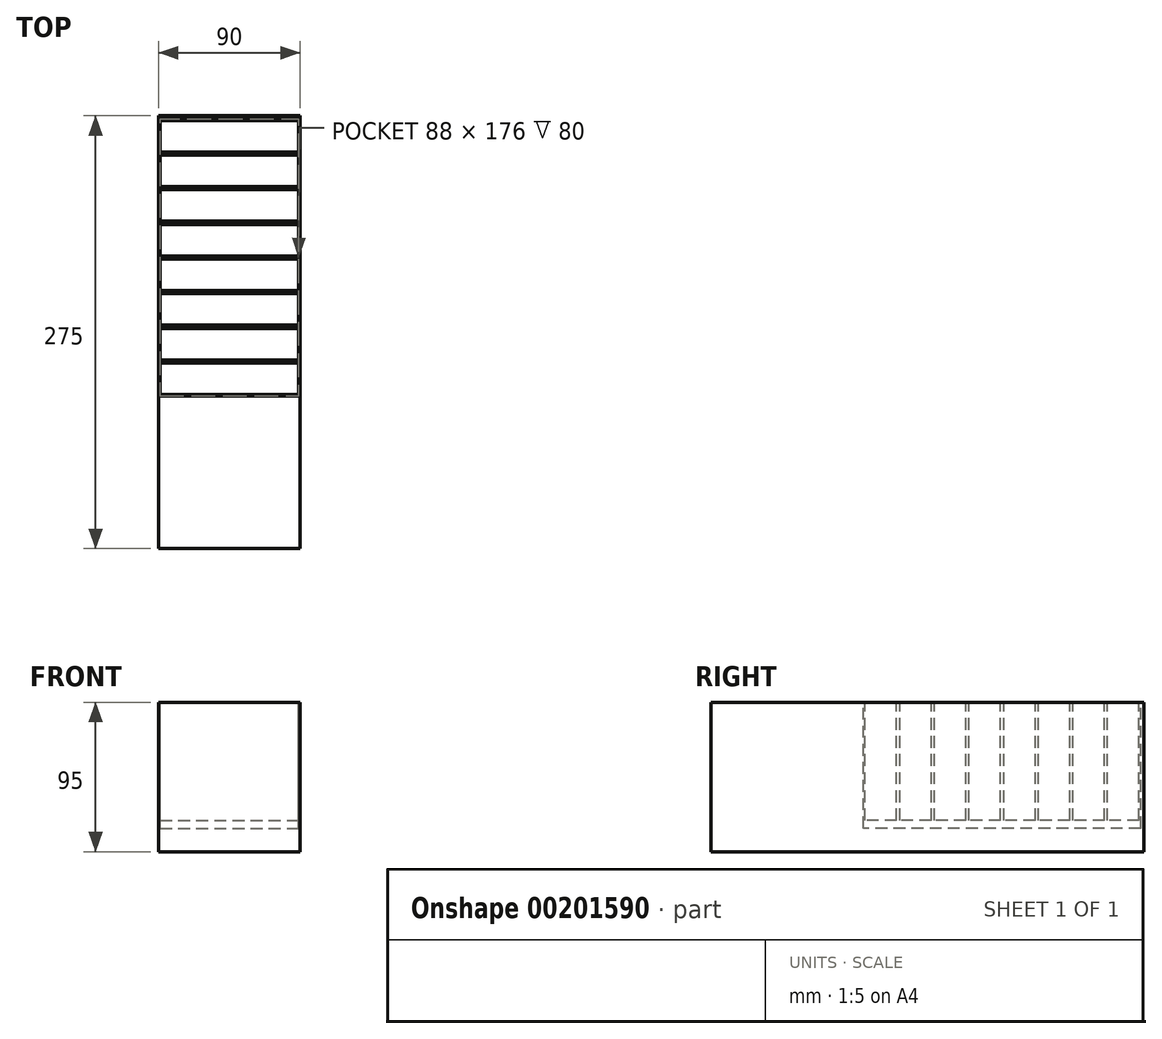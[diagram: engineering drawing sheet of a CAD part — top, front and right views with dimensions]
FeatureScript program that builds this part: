
annotation { "Feature Type Name" : "Feature", "Feature Type Description" : "" }
export const myFeature = defineFeature(function(context is Context, id is Id, definition is map)
    precondition{}
    {
        {
            var Q0;
            Q0=qCreatedBy(makeId("Front.planeOp"),FACE);
            var sketch = newSketch(context, id + "F0", { "sketchPlane" : qUnion([Q0])});
            skLineSegment(sketch, "E0.bottom", {"start": v(-45, 0) * mm, "end": v(45, 0) * mm});
            skLineSegment(sketch, "E0.top", {"start": v(-45, -95) * mm, "end": v(45, -95) * mm});
            skLineSegment(sketch, "E0.left", {"start": v(-45, 0) * mm, "end": v(-45, -95) * mm});
            skLineSegment(sketch, "E0.right", {"start": v(45, 0) * mm, "end": v(45, -95) * mm});
            skLineSegment(sketch, "E1", {"start": v(-45, 0) * mm, "end": v(45, -95) * mm, "construction": true});
            skSolve(sketch);
        }
        {
            var Q0;
            Q0 = qSketchRegion(id + "F0", true);
            extrude(context, id + "F1", {"entities" : qUnion([Q0]), "depth" : 275 * mm});
        }
        {
            var Q0;
            Q0=makeQuery(id+"F1.opExtrude","SWEPT_FACE",FACE,{"disambiguationData":[OSD([sQuery(id+"F0.wireOp",EDGE,"E0.bottom")])]});
            var sketch = newSketch(context, id + "F2", { "sketchPlane" : qUnion([Q0])});
            skLineSegment(sketch, "E2.bottom", {"start": v(-44, -2) * mm, "end": v(44, -2) * mm});
            skLineSegment(sketch, "E2.top", {"start": v(-44, -24) * mm, "end": v(44, -24) * mm, "construction": true});
            skLineSegment(sketch, "E2.left", {"start": v(-44, -2) * mm, "end": v(-44, -24) * mm});
            skLineSegment(sketch, "E2.right", {"start": v(44, -2) * mm, "end": v(44, -24) * mm});
            skLineSegment(sketch, "E3", {"start": v(-44, -24) * mm, "end": v(-44, -46) * mm});
            skLineSegment(sketch, "E4", {"start": v(-44, -46) * mm, "end": v(-44, -68) * mm});
            skLineSegment(sketch, "E5", {"start": v(-44, -68) * mm, "end": v(-44, -90) * mm});
            skLineSegment(sketch, "E6", {"start": v(-44, -90) * mm, "end": v(-44, -112) * mm});
            skLineSegment(sketch, "E7", {"start": v(-44, -112) * mm, "end": v(-44, -134) * mm});
            skLineSegment(sketch, "E8", {"start": v(-44, -134) * mm, "end": v(-44, -156) * mm});
            skLineSegment(sketch, "E9", {"start": v(-44, -156) * mm, "end": v(-44, -178) * mm});
            skLineSegment(sketch, "E10", {"start": v(0, 0) * mm, "end": v(0, -194.6) * mm, "construction": true});
            skLineSegment(sketch, "E11.MirrorCS", {"start": v(44, -156) * mm, "end": v(44, -178) * mm});
            skLineSegment(sketch, "E12.MirrorCS", {"start": v(44, -68) * mm, "end": v(44, -90) * mm});
            skLineSegment(sketch, "E13.MirrorCS", {"start": v(44, -24) * mm, "end": v(44, -46) * mm});
            skLineSegment(sketch, "E14.MirrorCS", {"start": v(44, -112) * mm, "end": v(44, -134) * mm});
            skLineSegment(sketch, "E15.MirrorCS", {"start": v(44, -134) * mm, "end": v(44, -156) * mm});
            skLineSegment(sketch, "E16.MirrorCS", {"start": v(44, -90) * mm, "end": v(44, -112) * mm});
            skLineSegment(sketch, "E17.MirrorCS", {"start": v(44, -46) * mm, "end": v(44, -68) * mm});
            skLineSegment(sketch, "E18", {"start": v(-44, -46) * mm, "end": v(44, -46) * mm, "construction": true});
            skLineSegment(sketch, "E19", {"start": v(-44, -68) * mm, "end": v(44, -68) * mm, "construction": true});
            skLineSegment(sketch, "E20", {"start": v(-44, -90) * mm, "end": v(44, -90) * mm, "construction": true});
            skLineSegment(sketch, "E21", {"start": v(-44, -112) * mm, "end": v(44, -112) * mm, "construction": true});
            skLineSegment(sketch, "E22", {"start": v(44, -134) * mm, "end": v(-44, -134) * mm, "construction": true});
            skLineSegment(sketch, "E23", {"start": v(-44, -156) * mm, "end": v(44, -156) * mm, "construction": true});
            skLineSegment(sketch, "E24", {"start": v(44, -178) * mm, "end": v(-44, -178) * mm});
            skSolve(sketch);
        }
        {
            var Q0;
            Q0 = qSketchRegion(id + "F2", true);
            extrude(context, id + "F3", {"entities" : qUnion([Q0]), "operationType" : NewBodyOperationType.REMOVE, "oppositeDirection" : true, "depth" : 80 * mm});
        }
        {
            var Q0;
            Q0=qCreatedBy(makeId("Top.planeOp"),FACE);
            var sketch = newSketch(context, id + "F4", { "sketchPlane" : qUnion([Q0])});
            skLineSegment(sketch, "E25.bottom", {"start": v(-44, -3) * mm, "end": v(44, -3) * mm});
            skLineSegment(sketch, "E25.top", {"start": v(-44, -23) * mm, "end": v(44, -23) * mm});
            skLineSegment(sketch, "E25.left", {"start": v(-44, -3) * mm, "end": v(-44, -23) * mm});
            skLineSegment(sketch, "E25.right", {"start": v(44, -3) * mm, "end": v(44, -23) * mm});
            skLineSegment(sketch, "E26", {"start": v(-44, -13) * mm, "end": v(44, -13) * mm, "construction": true});
            skLineSegment(sketch, "E27.0.1.0", {"start": v(-44, -25) * mm, "end": v(44, -25) * mm});
            skLineSegment(sketch, "E27.0.1.1", {"start": v(-44, -25) * mm, "end": v(-44, -45) * mm});
            skLineSegment(sketch, "E27.0.1.2", {"start": v(-44, -45) * mm, "end": v(44, -45) * mm});
            skLineSegment(sketch, "E27.0.1.3", {"start": v(44, -25) * mm, "end": v(44, -45) * mm});
            skLineSegment(sketch, "E27.0.2.0", {"start": v(-44, -47) * mm, "end": v(44, -47) * mm});
            skLineSegment(sketch, "E27.0.2.1", {"start": v(-44, -47) * mm, "end": v(-44, -67) * mm});
            skLineSegment(sketch, "E27.0.2.2", {"start": v(-44, -67) * mm, "end": v(44, -67) * mm});
            skLineSegment(sketch, "E27.0.2.3", {"start": v(44, -47) * mm, "end": v(44, -67) * mm});
            skLineSegment(sketch, "E27.0.3.0", {"start": v(-44, -69) * mm, "end": v(44, -69) * mm});
            skLineSegment(sketch, "E27.0.3.1", {"start": v(-44, -69) * mm, "end": v(-44, -89) * mm});
            skLineSegment(sketch, "E27.0.3.2", {"start": v(-44, -89) * mm, "end": v(44, -89) * mm});
            skLineSegment(sketch, "E27.0.3.3", {"start": v(44, -69) * mm, "end": v(44, -89) * mm});
            skLineSegment(sketch, "E27.0.4.0", {"start": v(-44, -91) * mm, "end": v(44, -91) * mm});
            skLineSegment(sketch, "E27.0.4.1", {"start": v(-44, -91) * mm, "end": v(-44, -111) * mm});
            skLineSegment(sketch, "E27.0.4.2", {"start": v(-44, -111) * mm, "end": v(44, -111) * mm});
            skLineSegment(sketch, "E27.0.4.3", {"start": v(44, -91) * mm, "end": v(44, -111) * mm});
            skLineSegment(sketch, "E27.0.5.0", {"start": v(-44, -113) * mm, "end": v(44, -113) * mm});
            skLineSegment(sketch, "E27.0.5.1", {"start": v(-44, -113) * mm, "end": v(-44, -133) * mm});
            skLineSegment(sketch, "E27.0.5.2", {"start": v(-44, -133) * mm, "end": v(44, -133) * mm});
            skLineSegment(sketch, "E27.0.5.3", {"start": v(44, -113) * mm, "end": v(44, -133) * mm});
            skLineSegment(sketch, "E27.0.6.0", {"start": v(-44, -135) * mm, "end": v(44, -135) * mm});
            skLineSegment(sketch, "E27.0.6.1", {"start": v(-44, -135) * mm, "end": v(-44, -155) * mm});
            skLineSegment(sketch, "E27.0.6.2", {"start": v(-44, -155) * mm, "end": v(44, -155) * mm});
            skLineSegment(sketch, "E27.0.6.3", {"start": v(44, -135) * mm, "end": v(44, -155) * mm});
            skLineSegment(sketch, "E27.0.7.0", {"start": v(-44, -157) * mm, "end": v(44, -157) * mm});
            skLineSegment(sketch, "E27.0.7.1", {"start": v(-44, -157) * mm, "end": v(-44, -177) * mm});
            skLineSegment(sketch, "E27.0.7.2", {"start": v(-44, -177) * mm, "end": v(44, -177) * mm});
            skLineSegment(sketch, "E27.0.7.3", {"start": v(44, -157) * mm, "end": v(44, -177) * mm});
            skLineSegment(sketch, "E27.direction1", {"start": v(-44, -3) * mm, "end": v(-19, -3) * mm, "construction": true});
            skLineSegment(sketch, "E27.direction2", {"start": v(-44, -3) * mm, "end": v(-44, -25) * mm, "construction": true});
            skSolve(sketch);
        }
        {
            var Q0;
            Q0 = qSketchRegion(id + "F4", true);
            extrude(context, id + "F5", {"entities" : qUnion([Q0]), "oppositeDirection" : true, "depth" : 75 * mm});
        }
    });
